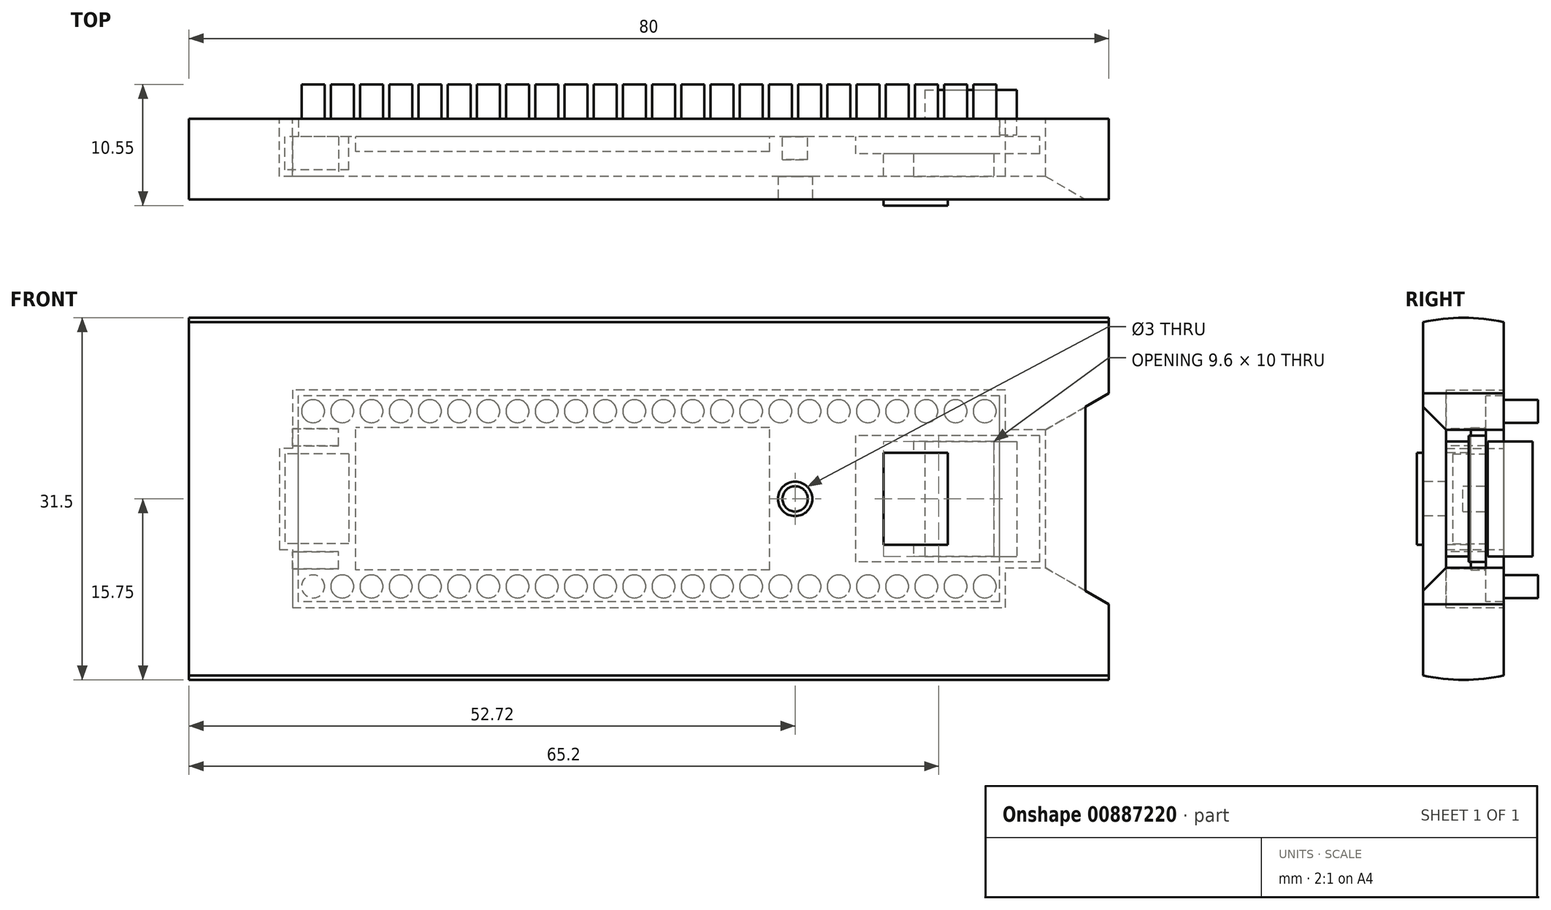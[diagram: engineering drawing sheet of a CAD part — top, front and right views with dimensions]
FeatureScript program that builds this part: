
annotation { "Feature Type Name" : "Feature", "Feature Type Description" : "" }
export const myFeature = defineFeature(function(context is Context, id is Id, definition is map)
    precondition{}
    {
        {
            var Q0;
            Q0=qCreatedBy(makeId("Front.planeOp"),FACE);
            var sketch = newSketch(context, id + "F0", { "sketchPlane" : qUnion([Q0])});
            skLineSegment(sketch, "E0.bottom", {"start": v(30.5, -8.95) * mm, "end": v(-30.5, -8.95) * mm});
            skLineSegment(sketch, "E0.top", {"start": v(30.5, 8.95) * mm, "end": v(-30.5, 8.95) * mm});
            skLineSegment(sketch, "E0.left", {"start": v(30.5, -8.95) * mm, "end": v(30.5, 8.95) * mm});
            skLineSegment(sketch, "E0.right", {"start": v(-30.5, -8.95) * mm, "end": v(-30.5, 8.95) * mm});
            skPoint(sketch, "E0.middle", {"position": v(0, 0) * mm});
            skCircle(sketch, "E1", {"center": v(12.72, 0) * mm, "radius": 1.1 * mm});
            skLineSegment(sketch, "E2.bottom", {"start": v(34, -5.5) * mm, "end": v(18, -5.5) * mm});
            skLineSegment(sketch, "E2.top", {"start": v(34, 5.5) * mm, "end": v(18, 5.5) * mm});
            skLineSegment(sketch, "E2.left", {"start": v(34, -5.5) * mm, "end": v(34, 5.5) * mm});
            skLineSegment(sketch, "E2.right", {"start": v(18, -5.5) * mm, "end": v(18, 5.5) * mm});
            skPoint(sketch, "E2.middle", {"position": v(26, 0) * mm});
            skLineSegment(sketch, "E3.bottom", {"start": v(-26.1, 3.9) * mm, "end": v(-31.65, 3.9) * mm});
            skLineSegment(sketch, "E3.top", {"start": v(-26.1, -3.9) * mm, "end": v(-31.65, -3.9) * mm});
            skLineSegment(sketch, "E3.left", {"start": v(-26.1, 3.9) * mm, "end": v(-26.1, -3.9) * mm});
            skLineSegment(sketch, "E3.right", {"start": v(-31.65, 3.9) * mm, "end": v(-31.65, -3.9) * mm});
            skPoint(sketch, "E3.middle", {"position": v(-28.87, 0) * mm});
            skLineSegment(sketch, "E4.bottom", {"start": v(10.5, -6.2) * mm, "end": v(-25.5, -6.2) * mm});
            skLineSegment(sketch, "E4.top", {"start": v(10.5, 6.2) * mm, "end": v(-25.5, 6.2) * mm});
            skLineSegment(sketch, "E4.left", {"start": v(10.5, -6.2) * mm, "end": v(10.5, 6.2) * mm});
            skLineSegment(sketch, "E4.right", {"start": v(-25.5, -6.2) * mm, "end": v(-25.5, 6.2) * mm});
            skPoint(sketch, "E4.middle", {"position": v(-7.5, 0) * mm});
            skSolve(sketch);
        }
        {
            var Q0;
            {var subQ8=sQuery(id+"F0.wireOp",EDGE,"E0.bottom");Q0=makeQuery(id+"F0.imprint","IMPRINT",FACE,{"disambiguationData":[TD([[makeQuery(id+"F0.imprint","IMPRINT",EDGE,{"derivedFrom":subQ8}),-1.0]])]});}
            var Q1;
            {var subQ5=sQuery(id+"F0.wireOp",EDGE,"E3.left");Q1=makeQuery(id+"F0.imprint","IMPRINT",FACE,{"disambiguationData":[TD([[makeQuery(id+"F0.imprint","IMPRINT",EDGE,{"derivedFrom":subQ5}),-1.0]])]});}
            var Q2;
            {var subQ5=sQuery(id+"F0.wireOp",EDGE,"E2.right");Q2=makeQuery(id+"F0.imprint","IMPRINT",FACE,{"disambiguationData":[TD([[makeQuery(id+"F0.imprint","IMPRINT",EDGE,{"derivedFrom":subQ5}),-1.0]])]});}
            var Q3;
            Q3=makeQuery(id+"F0.imprint","IMPRINT",FACE,{"disambiguationData":[TD([[makeQuery(id+"F0.imprint","IMPRINT",EDGE,{"derivedFrom":sQuery(id+"F0.wireOp",EDGE,"E1")}),1.0]])]});
            var Q4;
            Q4=makeQuery(id+"F0.imprint","IMPRINT",FACE,{"disambiguationData":[TD([[makeQuery(id+"F0.imprint","IMPRINT",EDGE,{"derivedFrom":sQuery(id+"F0.wireOp",EDGE,"E4.bottom")}),-1.0]])]});
            extrude(context, id + "F1", {"entities" : qUnion([Q0, Q1, Q2, Q3, Q4]), "oppositeDirection" : true, "depth" : 1.55 * mm, "offsetDistance" : 25 * mm});
        }
        {
            var Q0;
            Q0=makeQuery(id+"F0.imprint","IMPRINT",FACE,{"disambiguationData":[TD([[makeQuery(id+"F0.imprint","IMPRINT",EDGE,{"derivedFrom":sQuery(id+"F0.wireOp",EDGE,"E1")}),1.0]])]});
            extrude(context, id + "F2", {"entities" : qUnion([Q0]), "operationType" : NewBodyOperationType.ADD, "depth" : 2 * mm, "offsetDistance" : 25 * mm});
        }
        {
            var Q0;
            {var subQ5=sQuery(id+"F0.wireOp",EDGE,"E3.left");Q0=makeQuery(id+"F0.imprint","IMPRINT",FACE,{"disambiguationData":[TD([[makeQuery(id+"F0.imprint","IMPRINT",EDGE,{"derivedFrom":subQ5}),-1.0]])]});}
            var Q1;
            {var subQ5=sQuery(id+"F0.wireOp",EDGE,"E3.right");Q1=makeQuery(id+"F0.imprint","IMPRINT",FACE,{"disambiguationData":[TD([[makeQuery(id+"F0.imprint","IMPRINT",EDGE,{"derivedFrom":subQ5}),1.0]])]});}
            extrude(context, id + "F3", {"entities" : qUnion([Q0, Q1]), "operationType" : NewBodyOperationType.ADD, "depth" : 2.9 * mm, "offsetDistance" : 25 * mm});
        }
        {
            var Q0;
            {var subQ5=sQuery(id+"F0.wireOp",EDGE,"E2.left");Q0=makeQuery(id+"F0.imprint","IMPRINT",FACE,{"disambiguationData":[TD([[makeQuery(id+"F0.imprint","IMPRINT",EDGE,{"derivedFrom":subQ5}),1.0]])]});}
            var Q1;
            {var subQ5=sQuery(id+"F0.wireOp",EDGE,"E2.right");Q1=makeQuery(id+"F0.imprint","IMPRINT",FACE,{"disambiguationData":[TD([[makeQuery(id+"F0.imprint","IMPRINT",EDGE,{"derivedFrom":subQ5}),-1.0]])]});}
            extrude(context, id + "F4", {"entities" : qUnion([Q0, Q1]), "operationType" : NewBodyOperationType.ADD, "depth" : 1.5 * mm, "offsetDistance" : 25 * mm});
        }
        {
            var Q0;
            Q0=makeQuery(id+"F0.imprint","IMPRINT",FACE,{"disambiguationData":[TD([[makeQuery(id+"F0.imprint","IMPRINT",EDGE,{"derivedFrom":sQuery(id+"F0.wireOp",EDGE,"E4.bottom")}),-1.0]])]});
            extrude(context, id + "F5", {"entities" : qUnion([Q0]), "operationType" : NewBodyOperationType.ADD, "depth" : 1.3 * mm, "offsetDistance" : 25 * mm});
        }
        {
            var Q0;
            Q0=makeQuery(id+"F1.opExtrude","CAP_FACE",FACE,{"disambiguationData":[OSD([sQuery(id+"F0.wireOp",EDGE,"E0.bottom"),sQuery(id+"F0.wireOp",EDGE,"E0.top"),sQuery(id+"F0.wireOp",EDGE,"E0.left"),sQuery(id+"F0.wireOp",EDGE,"E0.right")])],"isStart":false});
            var sketch = newSketch(context, id + "F6", { "sketchPlane" : qUnion([Q0])});
            skCircle(sketch, "E5", {"center": v(29.21, -7.62) * mm, "radius": 1 * mm});
            skCircle(sketch, "E6.0.1.0", {"center": v(29.21, 7.62) * mm, "radius": 1 * mm});
            skCircle(sketch, "E6.1.0.0", {"center": v(26.67, -7.62) * mm, "radius": 1 * mm});
            skCircle(sketch, "E6.1.1.0", {"center": v(26.67, 7.62) * mm, "radius": 1 * mm});
            skCircle(sketch, "E6.2.0.0", {"center": v(24.13, -7.62) * mm, "radius": 1 * mm});
            skCircle(sketch, "E6.2.1.0", {"center": v(24.13, 7.62) * mm, "radius": 1 * mm});
            skCircle(sketch, "E6.3.0.0", {"center": v(21.6, -7.62) * mm, "radius": 1 * mm});
            skCircle(sketch, "E6.3.1.0", {"center": v(21.6, 7.62) * mm, "radius": 1 * mm});
            skCircle(sketch, "E6.4.0.0", {"center": v(19.05, -7.62) * mm, "radius": 1 * mm});
            skCircle(sketch, "E6.4.1.0", {"center": v(19.05, 7.62) * mm, "radius": 1 * mm});
            skCircle(sketch, "E6.5.0.0", {"center": v(16.51, -7.62) * mm, "radius": 1 * mm});
            skCircle(sketch, "E6.5.1.0", {"center": v(16.51, 7.62) * mm, "radius": 1 * mm});
            skCircle(sketch, "E6.6.0.0", {"center": v(13.97, -7.62) * mm, "radius": 1 * mm});
            skCircle(sketch, "E6.6.1.0", {"center": v(13.97, 7.62) * mm, "radius": 1 * mm});
            skCircle(sketch, "E6.7.0.0", {"center": v(11.43, -7.62) * mm, "radius": 1 * mm});
            skCircle(sketch, "E6.7.1.0", {"center": v(11.43, 7.62) * mm, "radius": 1 * mm});
            skCircle(sketch, "E6.8.0.0", {"center": v(8.9, -7.62) * mm, "radius": 1 * mm});
            skCircle(sketch, "E6.8.1.0", {"center": v(8.9, 7.62) * mm, "radius": 1 * mm});
            skCircle(sketch, "E6.9.0.0", {"center": v(6.35, -7.62) * mm, "radius": 1 * mm});
            skCircle(sketch, "E6.9.1.0", {"center": v(6.35, 7.62) * mm, "radius": 1 * mm});
            skCircle(sketch, "E6.10.0.0", {"center": v(3.81, -7.62) * mm, "radius": 1 * mm});
            skCircle(sketch, "E6.10.1.0", {"center": v(3.81, 7.62) * mm, "radius": 1 * mm});
            skCircle(sketch, "E6.11.0.0", {"center": v(1.27, -7.62) * mm, "radius": 1 * mm});
            skCircle(sketch, "E6.11.1.0", {"center": v(1.27, 7.62) * mm, "radius": 1 * mm});
            skCircle(sketch, "E6.12.0.0", {"center": v(-1.27, -7.62) * mm, "radius": 1 * mm});
            skCircle(sketch, "E6.12.1.0", {"center": v(-1.27, 7.62) * mm, "radius": 1 * mm});
            skCircle(sketch, "E6.13.0.0", {"center": v(-3.81, -7.62) * mm, "radius": 1 * mm});
            skCircle(sketch, "E6.13.1.0", {"center": v(-3.81, 7.62) * mm, "radius": 1 * mm});
            skCircle(sketch, "E6.14.0.0", {"center": v(-6.35, -7.62) * mm, "radius": 1 * mm});
            skCircle(sketch, "E6.14.1.0", {"center": v(-6.35, 7.62) * mm, "radius": 1 * mm});
            skCircle(sketch, "E6.15.0.0", {"center": v(-8.9, -7.62) * mm, "radius": 1 * mm});
            skCircle(sketch, "E6.15.1.0", {"center": v(-8.9, 7.62) * mm, "radius": 1 * mm});
            skCircle(sketch, "E6.16.0.0", {"center": v(-11.43, -7.62) * mm, "radius": 1 * mm});
            skCircle(sketch, "E6.16.1.0", {"center": v(-11.43, 7.62) * mm, "radius": 1 * mm});
            skCircle(sketch, "E6.17.0.0", {"center": v(-13.97, -7.62) * mm, "radius": 1 * mm});
            skCircle(sketch, "E6.17.1.0", {"center": v(-13.97, 7.62) * mm, "radius": 1 * mm});
            skCircle(sketch, "E6.18.0.0", {"center": v(-16.51, -7.62) * mm, "radius": 1 * mm});
            skCircle(sketch, "E6.18.1.0", {"center": v(-16.51, 7.62) * mm, "radius": 1 * mm});
            skCircle(sketch, "E6.19.0.0", {"center": v(-19.05, -7.62) * mm, "radius": 1 * mm});
            skCircle(sketch, "E6.19.1.0", {"center": v(-19.05, 7.62) * mm, "radius": 1 * mm});
            skCircle(sketch, "E6.20.0.0", {"center": v(-21.6, -7.62) * mm, "radius": 1 * mm});
            skCircle(sketch, "E6.20.1.0", {"center": v(-21.6, 7.62) * mm, "radius": 1 * mm});
            skCircle(sketch, "E6.21.0.0", {"center": v(-24.13, -7.62) * mm, "radius": 1 * mm});
            skCircle(sketch, "E6.21.1.0", {"center": v(-24.13, 7.62) * mm, "radius": 1 * mm});
            skCircle(sketch, "E6.22.0.0", {"center": v(-26.67, -7.62) * mm, "radius": 1 * mm});
            skCircle(sketch, "E6.22.1.0", {"center": v(-26.67, 7.62) * mm, "radius": 1 * mm});
            skCircle(sketch, "E6.23.0.0", {"center": v(-29.21, -7.62) * mm, "radius": 1 * mm});
            skCircle(sketch, "E6.23.1.0", {"center": v(-29.21, 7.62) * mm, "radius": 1 * mm});
            skLineSegment(sketch, "E6.direction1", {"start": v(29.21, -7.62) * mm, "end": v(26.67, -7.62) * mm, "construction": true});
            skLineSegment(sketch, "E6.direction2", {"start": v(29.21, -7.62) * mm, "end": v(29.21, 7.62) * mm, "construction": true});
            skSolve(sketch);
        }
        {
            var Q0;
            Q0=qSketchRegion(id+"F6",true);
            extrude(context, id + "F7", {"entities" : qUnion([Q0]), "operationType" : NewBodyOperationType.ADD, "depth" : 3 * mm, "offsetDistance" : 25 * mm});
        }
        {
            var Q0;
            Q0=makeQuery(id+"F4.opExtrude","CAP_FACE",FACE,{"disambiguationData":[OSD([sQuery(id+"F0.wireOp",EDGE,"E2.bottom"),sQuery(id+"F0.wireOp",EDGE,"E2.top"),sQuery(id+"F0.wireOp",EDGE,"E2.left"),sQuery(id+"F0.wireOp",EDGE,"E2.right")])],"isStart":false});
            var sketch = newSketch(context, id + "F8", { "sketchPlane" : qUnion([Q0])});
            skLineSegment(sketch, "E7.bottom", {"start": v(26, -4) * mm, "end": v(20.4, -4) * mm});
            skLineSegment(sketch, "E7.top", {"start": v(26, 4) * mm, "end": v(20.4, 4) * mm});
            skLineSegment(sketch, "E7.left", {"start": v(26, -4) * mm, "end": v(26, 4) * mm});
            skLineSegment(sketch, "E7.right", {"start": v(20.4, -4) * mm, "end": v(20.4, 4) * mm});
            skPoint(sketch, "E7.middle", {"position": v(23.2, 0) * mm});
            skSolve(sketch);
        }
        {
            var Q0;
            Q0=makeQuery(id+"F1.opExtrude","CAP_FACE",FACE,{"disambiguationData":[OSD([sQuery(id+"F0.wireOp",EDGE,"E0.bottom"),sQuery(id+"F0.wireOp",EDGE,"E0.top"),sQuery(id+"F0.wireOp",EDGE,"E0.left"),sQuery(id+"F0.wireOp",EDGE,"E0.right")])],"isStart":false});
            var sketch = newSketch(context, id + "F9", { "sketchPlane" : qUnion([Q0])});
            skLineSegment(sketch, "E8.bottom", {"start": v(-24, 5) * mm, "end": v(-32, 5) * mm});
            skLineSegment(sketch, "E8.top", {"start": v(-24, -5) * mm, "end": v(-32, -5) * mm});
            skLineSegment(sketch, "E8.left", {"start": v(-24, 5) * mm, "end": v(-24, -5) * mm});
            skLineSegment(sketch, "E8.right", {"start": v(-32, 5) * mm, "end": v(-32, -5) * mm});
            skPoint(sketch, "E8.middle", {"position": v(-28, 0) * mm});
            skLineSegment(sketch, "E9", {"start": v(-30.5, -5) * mm, "end": v(-30.5, 5) * mm});
            skSolve(sketch);
        }
        {
            var Q0;
            Q0=makeQuery(id+"F8.imprint","IMPRINT",FACE,{"disambiguationData":[TD([[makeQuery(id+"F8.imprint","IMPRINT",EDGE,{"derivedFrom":sQuery(id+"F8.wireOp",EDGE,"E7.bottom")}),-1.0]])]});
            extrude(context, id + "F10", {"entities" : qUnion([Q0]), "depth" : 4.5 * mm, "offsetDistance" : 25 * mm});
        }
        {
            var Q0;
            {var subQ0=sQuery(id+"F9.wireOp",EDGE,"E8.right");Q0=makeQuery(id+"F9.imprint","IMPRINT",FACE,{"disambiguationData":[TD([[makeQuery(id+"F9.imprint","IMPRINT",EDGE,{"derivedFrom":subQ0}),1.0]])]});}
            extrude(context, id + "F11", {"entities" : qUnion([Q0]), "oppositeDirection" : true, "depth" : 1.4 * mm, "offsetDistance" : 25 * mm});
        }
        {
            var Q0;
            {var subQ0=sQuery(id+"F9.wireOp",EDGE,"E8.right");Q0=makeQuery(id+"F9.imprint","IMPRINT",FACE,{"disambiguationData":[TD([[makeQuery(id+"F9.imprint","IMPRINT",EDGE,{"derivedFrom":subQ0}),1.0]])]});}
            var Q1;
            {var subQ0=sQuery(id+"F9.wireOp",EDGE,"E8.left");Q1=makeQuery(id+"F9.imprint","IMPRINT",FACE,{"disambiguationData":[TD([[makeQuery(id+"F9.imprint","IMPRINT",EDGE,{"derivedFrom":subQ0}),-1.0]])]});}
            extrude(context, id + "F12", {"entities" : qUnion([Q0, Q1]), "operationType" : NewBodyOperationType.ADD, "depth" : 2.5 * mm, "offsetDistance" : 25 * mm});
        }
        {
            var Q0;
            {var subQ1=sQuery(id+"F9.wireOp",EDGE,"E8.left");Q0=makeQuery(id+"F9.imprint","IMPRINT",FACE,{"disambiguationData":[TD([[makeQuery(id+"F9.imprint","IMPRINT",EDGE,{"derivedFrom":subQ1}),1.0]])]});}
            var sketch = newSketch(context, id + "F13", { "sketchPlane" : qUnion([Q0])});
            skLineSegment(sketch, "E10.bottom", {"start": v(-40, -17.5) * mm, "end": v(40, -17.5) * mm});
            skLineSegment(sketch, "E10.top", {"start": v(-40, 17.5) * mm, "end": v(40, 17.5) * mm});
            skLineSegment(sketch, "E10.left", {"start": v(-40, -17.5) * mm, "end": v(-40, 17.5) * mm});
            skLineSegment(sketch, "E10.right", {"start": v(40, -17.5) * mm, "end": v(40, 17.5) * mm});
            skPoint(sketch, "E10.middle", {"position": v(0, 0) * mm});
            skLineSegment(sketch, "E11", {"start": v(30.5, 8.95) * mm, "end": v(30.5, 3.9) * mm, "construction": true});
            skLineSegment(sketch, "E12", {"start": v(30.5, 3.9) * mm, "end": v(31.65, 3.9) * mm, "construction": true});
            skLineSegment(sketch, "E13", {"start": v(31.65, 3.9) * mm, "end": v(31.65, -3.9) * mm, "construction": true});
            skLineSegment(sketch, "E14", {"start": v(31.65, -3.9) * mm, "end": v(30.5, -3.9) * mm, "construction": true});
            skLineSegment(sketch, "E15", {"start": v(30.5, -3.9) * mm, "end": v(30.5, -8.95) * mm, "construction": true});
            skLineSegment(sketch, "E16", {"start": v(30.5, -8.95) * mm, "end": v(-30.5, -8.95) * mm, "construction": true});
            skLineSegment(sketch, "E17", {"start": v(-30.5, -8.95) * mm, "end": v(-30.5, -5.5) * mm, "construction": true});
            skLineSegment(sketch, "E18", {"start": v(-30.5, -5.5) * mm, "end": v(-34, -5.5) * mm, "construction": true});
            skLineSegment(sketch, "E19", {"start": v(-34, -5.5) * mm, "end": v(-34, 5.5) * mm, "construction": true});
            skLineSegment(sketch, "E20", {"start": v(-34, 5.5) * mm, "end": v(-30.5, 5.5) * mm, "construction": true});
            skLineSegment(sketch, "E21", {"start": v(-30.5, 5.5) * mm, "end": v(-30.5, 8.95) * mm, "construction": true});
            skLineSegment(sketch, "E22", {"start": v(-30.5, 8.95) * mm, "end": v(30.5, 8.95) * mm, "construction": true});
            skLineSegment(sketch, "E23.0", {"start": v(-31, 6) * mm, "end": v(-31, 9.45) * mm});
            skLineSegment(sketch, "E23.1", {"start": v(32.15, -4.4) * mm, "end": v(31, -4.4) * mm});
            skLineSegment(sketch, "E23.2", {"start": v(32.15, 4.4) * mm, "end": v(32.15, -4.4) * mm});
            skLineSegment(sketch, "E23.3", {"start": v(31, 4.4) * mm, "end": v(32.15, 4.4) * mm});
            skLineSegment(sketch, "E23.4", {"start": v(31, 9.45) * mm, "end": v(31, 4.4) * mm});
            skLineSegment(sketch, "E23.5", {"start": v(31, -4.4) * mm, "end": v(31, -9.45) * mm});
            skLineSegment(sketch, "E23.6", {"start": v(-31, 9.45) * mm, "end": v(31, 9.45) * mm});
            skLineSegment(sketch, "E23.7", {"start": v(31, -9.45) * mm, "end": v(-31, -9.45) * mm});
            skLineSegment(sketch, "E23.8", {"start": v(-31, -9.45) * mm, "end": v(-31, -6) * mm});
            skLineSegment(sketch, "E23.9", {"start": v(-31, -6) * mm, "end": v(-34.5, -6) * mm});
            skLineSegment(sketch, "E23.10", {"start": v(-34.5, -6) * mm, "end": v(-34.5, 6) * mm});
            skLineSegment(sketch, "E23.11", {"start": v(-34.5, 6) * mm, "end": v(-31, 6) * mm});
            skLineSegment(sketch, "E24", {"start": v(31, 4.4) * mm, "end": v(31, -4.4) * mm});
            skLineSegment(sketch, "E25", {"start": v(-31, 6) * mm, "end": v(-31, -6) * mm});
            skLineSegment(sketch, "E26.bottom", {"start": v(27, 2.25) * mm, "end": v(29.5, 2.25) * mm});
            skLineSegment(sketch, "E26.top", {"start": v(27, -2.25) * mm, "end": v(29.5, -2.25) * mm});
            skLineSegment(sketch, "E26.left", {"start": v(27, 2.25) * mm, "end": v(27, -2.25) * mm});
            skLineSegment(sketch, "E26.right", {"start": v(29.5, 2.25) * mm, "end": v(29.5, -2.25) * mm});
            skPoint(sketch, "E26.middle", {"position": v(28.25, 0) * mm});
            skLineSegment(sketch, "E27.bottom", {"start": v(-25.25, -3.75) * mm, "end": v(-20.75, -3.75) * mm});
            skLineSegment(sketch, "E27.top", {"start": v(-25.25, 3.75) * mm, "end": v(-20.75, 3.75) * mm});
            skLineSegment(sketch, "E27.left", {"start": v(-25.25, -3.75) * mm, "end": v(-25.25, 3.75) * mm});
            skLineSegment(sketch, "E27.right", {"start": v(-20.75, -3.75) * mm, "end": v(-20.75, 3.75) * mm});
            skPoint(sketch, "E27.middle", {"position": v(-23, 0) * mm});
            skSolve(sketch);
        }
        {
            var Q0;
            Q0=makeQuery(id+"F13.imprint","IMPRINT",FACE,{"disambiguationData":[TD([[makeQuery(id+"F13.imprint","IMPRINT",EDGE,{"derivedFrom":sQuery(id+"F13.wireOp",EDGE,"E10.bottom")}),1.0]])]});
            extrude(context, id + "F14", {"entities" : qUnion([Q0]), "oppositeDirection" : true, "depth" : 7 * mm, "offsetDistance" : 25 * mm});
        }
        {
            var Q0;
            Q0=makeQuery(id+"F14.opExtrude","CAP_FACE",FACE,{"disambiguationData":[OSD([sQuery(id+"F13.wireOp",EDGE,"E10.bottom"),sQuery(id+"F13.wireOp",EDGE,"E10.top"),sQuery(id+"F13.wireOp",EDGE,"E10.left"),sQuery(id+"F13.wireOp",EDGE,"E10.right"),sQuery(id+"F13.wireOp",EDGE,"E23.0"),sQuery(id+"F13.wireOp",EDGE,"E23.1"),sQuery(id+"F13.wireOp",EDGE,"E23.2"),sQuery(id+"F13.wireOp",EDGE,"E23.3"),sQuery(id+"F13.wireOp",EDGE,"E23.4"),sQuery(id+"F13.wireOp",EDGE,"E23.5"),sQuery(id+"F13.wireOp",EDGE,"E23.6"),sQuery(id+"F13.wireOp",EDGE,"E23.7"),sQuery(id+"F13.wireOp",EDGE,"E23.8"),sQuery(id+"F13.wireOp",EDGE,"E23.9"),sQuery(id+"F13.wireOp",EDGE,"E23.10"),sQuery(id+"F13.wireOp",EDGE,"E23.11")])],"isStart":false});
            var sketch = newSketch(context, id + "F15", { "sketchPlane" : qUnion([Q0])});
            skLineSegment(sketch, "E28.bottom", {"start": v(-31, 6.1) * mm, "end": v(-27, 6.1) * mm});
            skLineSegment(sketch, "E28.top", {"start": v(-31, 4.6) * mm, "end": v(-27, 4.6) * mm});
            skLineSegment(sketch, "E28.left", {"start": v(-31, 6.1) * mm, "end": v(-31, 4.6) * mm});
            skLineSegment(sketch, "E28.right", {"start": v(-27, 6.1) * mm, "end": v(-27, 4.6) * mm});
            skLineSegment(sketch, "E29.bottom", {"start": v(-27, -4.6) * mm, "end": v(-31, -4.6) * mm});
            skLineSegment(sketch, "E29.top", {"start": v(-27, -6.1) * mm, "end": v(-31, -6.1) * mm});
            skLineSegment(sketch, "E29.left", {"start": v(-27, -4.6) * mm, "end": v(-27, -6.1) * mm});
            skLineSegment(sketch, "E29.right", {"start": v(-31, -4.6) * mm, "end": v(-31, -6.1) * mm});
            skLineSegment(sketch, "E30.bottom", {"start": v(23, -5) * mm, "end": v(30, -5) * mm});
            skLineSegment(sketch, "E30.top", {"start": v(23, 5) * mm, "end": v(30, 5) * mm});
            skLineSegment(sketch, "E30.left", {"start": v(23, -5) * mm, "end": v(23, 5) * mm});
            skLineSegment(sketch, "E30.right", {"start": v(30, -5) * mm, "end": v(30, 5) * mm});
            skPoint(sketch, "E30.middle", {"position": v(26.5, 0) * mm});
            skSolve(sketch);
        }
        {
            var Q0;
            Q0=makeQuery(id+"F15.imprint","IMPRINT",FACE,{"disambiguationData":[TD([[makeQuery(id+"F15.imprint","IMPRINT",EDGE,{"derivedFrom":makeQuery(id+"F14.opExtrude","CAP_EDGE",EDGE,{"disambiguationData":[OSD([sQuery(id+"F13.wireOp",EDGE,"E23.0")])],"isStart":false})}),1.0]])]});
            extrude(context, id + "F16", {"entities" : qUnion([Q0]), "operationType" : NewBodyOperationType.ADD, "oppositeDirection" : true, "depth" : 2 * mm, "offsetDistance" : 25 * mm});
        }
        {
            var Q0;
            Q0=makeQuery(id+"F15.imprint","IMPRINT",FACE,{"disambiguationData":[TD([[makeQuery(id+"F15.imprint","IMPRINT",EDGE,{"derivedFrom":sQuery(id+"F15.wireOp",EDGE,"E28.bottom")}),-1.0]])]});
            var Q1;
            Q1=makeQuery(id+"F15.imprint","IMPRINT",FACE,{"disambiguationData":[TD([[makeQuery(id+"F15.imprint","IMPRINT",EDGE,{"derivedFrom":sQuery(id+"F15.wireOp",EDGE,"E29.bottom")}),1.0]])]});
            var Q2;
            Q2=makeQuery(id+"F1.opExtrude","CAP_FACE",FACE,{"disambiguationData":[OSD([sQuery(id+"F0.wireOp",EDGE,"E0.bottom"),sQuery(id+"F0.wireOp",EDGE,"E0.top"),sQuery(id+"F0.wireOp",EDGE,"E0.left"),sQuery(id+"F0.wireOp",EDGE,"E0.right")])],"isStart":true});
            extrude(context, id + "F17", {"entities" : qUnion([Q0, Q1]), "operationType" : NewBodyOperationType.ADD, "endBound" : BoundingType.UP_TO_SURFACE, "oppositeDirection" : true, "depth" : 5 * mm, "endBoundEntityFace" : qUnion([Q2]), "offsetDistance" : 25 * mm});
        }
        {
            var Q0;
            Q0=makeQuery(id+"F15.imprint","IMPRINT",FACE,{"disambiguationData":[TD([[makeQuery(id+"F15.imprint","IMPRINT",EDGE,{"derivedFrom":sQuery(id+"F15.wireOp",EDGE,"E30.bottom")}),1.0]])]});
            var Q1;
            Q1=makeQuery(id+"F4.opExtrude","CAP_FACE",FACE,{"disambiguationData":[OSD([sQuery(id+"F0.wireOp",EDGE,"E2.bottom"),sQuery(id+"F0.wireOp",EDGE,"E2.top"),sQuery(id+"F0.wireOp",EDGE,"E2.left"),sQuery(id+"F0.wireOp",EDGE,"E2.right")])],"isStart":false});
            extrude(context, id + "F18", {"entities" : qUnion([Q0]), "operationType" : NewBodyOperationType.ADD, "endBound" : BoundingType.UP_TO_SURFACE, "oppositeDirection" : true, "depth" : 25 * mm, "endBoundEntityFace" : qUnion([Q1]), "offsetDistance" : 25 * mm});
        }
        {
            var Q0;
            {var subQ3=sQuery(id+"F15.wireOp",EDGE,"E28.left");Q0=makeQuery(id+"F15.imprint","IMPRINT",FACE,{"disambiguationData":[TD([[makeQuery(id+"F15.imprint","IMPRINT",EDGE,{"derivedFrom":subQ3}),-1.0]])]});}
            var sketch = newSketch(context, id + "F19", { "sketchPlane" : qUnion([Q0])});
            skCircle(sketch, "E31", {"center": v(12.72, 0) * mm, "radius": 1.5 * mm});
            skSolve(sketch);
        }
        {
            var Q0;
            Q0=makeQuery(id+"F19.imprint","IMPRINT",FACE,{"disambiguationData":[TD([[makeQuery(id+"F19.imprint","IMPRINT",EDGE,{"derivedFrom":sQuery(id+"F19.wireOp",EDGE,"E31")}),1.0]])]});
            extrude(context, id + "F20", {"entities" : qUnion([Q0]), "operationType" : NewBodyOperationType.REMOVE, "endBound" : BoundingType.UP_TO_NEXT, "oppositeDirection" : true, "depth" : 25 * mm, "offsetDistance" : 25 * mm});
        }
        {
            var Q0;
            Q0=makeQuery(id+"F14.opExtrude","SWEPT_FACE",FACE,{"disambiguationData":[OSD([sQuery(id+"F13.wireOp",EDGE,"E23.10")])]});
            var sketch = newSketch(context, id + "F21", { "sketchPlane" : qUnion([Q0])});
            skLineSegment(sketch, "E32.bottom", {"start": v(1.5, -5.5) * mm, "end": v(0, -5.5) * mm, "construction": true});
            skLineSegment(sketch, "E32.top", {"start": v(1.5, 5.5) * mm, "end": v(0, 5.5) * mm, "construction": true});
            skLineSegment(sketch, "E32.left", {"start": v(1.5, -5.5) * mm, "end": v(1.5, 5.5) * mm, "construction": true});
            skLineSegment(sketch, "E32.right", {"start": v(0, -5.5) * mm, "end": v(0, 5.5) * mm, "construction": true});
            skLineSegment(sketch, "E33.0", {"start": v(4.5, -8.5) * mm, "end": v(4.5, 8.5) * mm});
            skLineSegment(sketch, "E33.1", {"start": v(4.5, -8.5) * mm, "end": v(-3, -8.5) * mm});
            skLineSegment(sketch, "E33.2", {"start": v(-3, -8.5) * mm, "end": v(-3, 8.5) * mm});
            skLineSegment(sketch, "E33.3", {"start": v(4.5, 8.5) * mm, "end": v(-3, 8.5) * mm});
            skSolve(sketch);
        }
        {
            var Q0;
            {var subQ0=sQuery(id+"F13.wireOp",EDGE,"E23.10");Q0=makeQuery(id+"F21.imprint","IMPRINT",FACE,{"disambiguationData":[TD([[makeQuery(id+"F21.imprint","IMPRINT",EDGE,{"derivedFrom":makeQuery(id+"F14.opExtrude","CAP_EDGE",EDGE,{"disambiguationData":[OSD([subQ0])],"isStart":true})}),-1.0]])]});}
            var Q1;
            Q1=makeQuery(id+"F14.opExtrude","SWEPT_FACE",FACE,{"disambiguationData":[OSD([sQuery(id+"F13.wireOp",EDGE,"E10.left")])]});
            extrude(context, id + "F22", {"entities" : qUnion([Q0]), "operationType" : NewBodyOperationType.REMOVE, "endBound" : BoundingType.UP_TO_SURFACE, "oppositeDirection" : true, "depth" : 25 * mm, "endBoundEntityFace" : qUnion([Q1]), "offsetDistance" : 25 * mm, "hasDraft" : true, "draftAngle" : 30 * degree});
        }
        {
            var Q0;
            Q0=makeQuery(id+"F14.opExtrude","SWEPT_FACE",FACE,{"disambiguationData":[OSD([sQuery(id+"F13.wireOp",EDGE,"E10.right")])]});
            var sketch = newSketch(context, id + "F23", { "sketchPlane" : qUnion([Q0])});
            skArc(sketch, "E34", {"start": v(-1.55, -15.36) * mm, "mid": v(1.95, -15.75) * mm, "end": v(5.45, -15.36) * mm});
            skLineSegment(sketch, "E35.bottom", {"start": v(-1.55, 17.5) * mm, "end": v(5.45, 17.5) * mm});
            skLineSegment(sketch, "E35.top", {"start": v(-1.55, -17.5) * mm, "end": v(5.45, -17.5) * mm});
            skLineSegment(sketch, "E35.left", {"start": v(-1.55, 17.5) * mm, "end": v(-1.55, 15.36) * mm});
            skLineSegment(sketch, "E35.right", {"start": v(5.45, 17.5) * mm, "end": v(5.45, 15.36) * mm});
            skArc(sketch, "E36.trimOffspring", {"start": v(5.45, 15.36) * mm, "mid": v(1.95, 15.75) * mm, "end": v(-1.55, 15.36) * mm});
            skLineSegment(sketch, "E37.trimOffspring", {"start": v(5.45, -15.36) * mm, "end": v(5.45, -17.5) * mm});
            skLineSegment(sketch, "E38.trimOffspring", {"start": v(-1.55, -15.36) * mm, "end": v(-1.55, -17.5) * mm});
            skPoint(sketch, "E39.orphan", {"position": v(5.45, 0) * mm});
            skPoint(sketch, "E40.start.orphan", {"position": v(-1.55, 0) * mm});
            skSolve(sketch);
        }
        {
            var Q0;
            Q0 = qSketchRegion(id + "F23", true);
            extrude(context, id + "F24", {"entities" : qUnion([Q0]), "operationType" : NewBodyOperationType.REMOVE, "oppositeDirection" : true, "depth" : 80 * mm, "offsetDistance" : 25 * mm});
        }
    });
